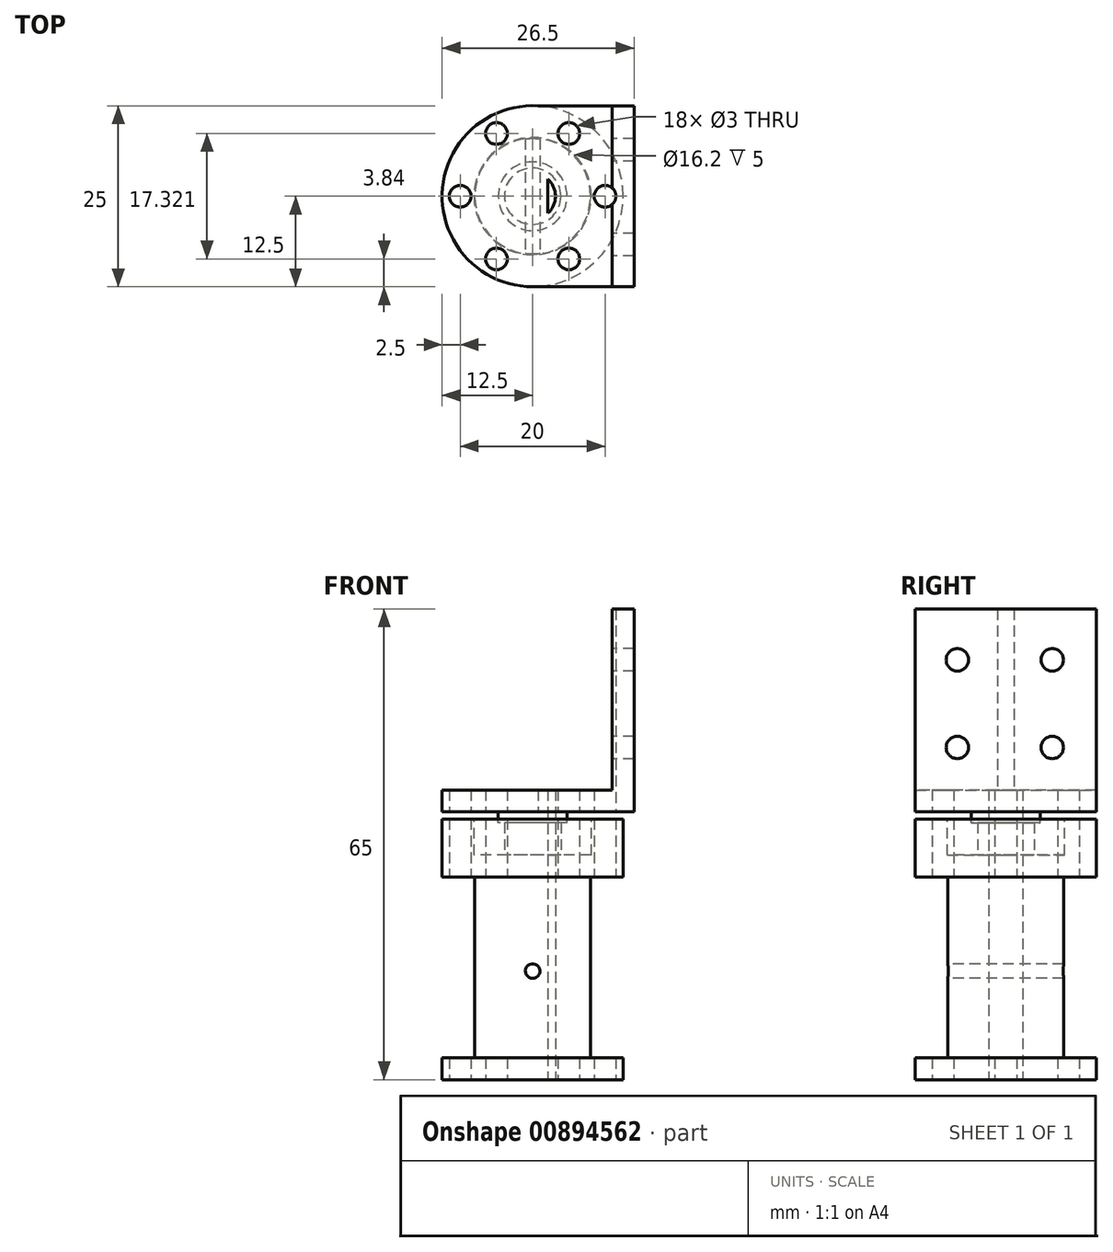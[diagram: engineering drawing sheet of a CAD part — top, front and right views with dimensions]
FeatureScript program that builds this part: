
annotation { "Feature Type Name" : "Feature", "Feature Type Description" : "" }
export const myFeature = defineFeature(function(context is Context, id is Id, definition is map)
    precondition{}
    {
        {
            var Q0;
            Q0=qCreatedBy(makeId("Top.planeOp"),FACE);
            var sketch = newSketch(context, id + "F0", { "sketchPlane" : qUnion([Q0])});
            skCircle(sketch, "E0", {"center": v(0, 0) * mm, "radius": 12.5 * mm});
            skLineSegment(sketch, "E1", {"start": v(0, 0) * mm, "end": v(10, 0) * mm, "construction": true});
            skCircle(sketch, "E2", {"center": v(10, 0) * mm, "radius": 1.5 * mm});
            skCircle(sketch, "E3.1.0", {"center": v(5, 8.66) * mm, "radius": 1.5 * mm});
            skCircle(sketch, "E3.2.0", {"center": v(-5, 8.66) * mm, "radius": 1.5 * mm});
            skCircle(sketch, "E3.3.0", {"center": v(-10, 0) * mm, "radius": 1.5 * mm});
            skCircle(sketch, "E3.4.0", {"center": v(-5, -8.66) * mm, "radius": 1.5 * mm});
            skCircle(sketch, "E3.5.0", {"center": v(5, -8.66) * mm, "radius": 1.5 * mm});
            skCircle(sketch, "E4", {"center": v(0, 0) * mm, "radius": 3.15 * mm});
            skLineSegment(sketch, "E5.bottom", {"start": v(2.1, -4.87) * mm, "end": v(-8.4, -4.87) * mm, "construction": true});
            skLineSegment(sketch, "E5.top", {"start": v(2.1, 4.87) * mm, "end": v(-8.4, 4.87) * mm, "construction": true});
            skLineSegment(sketch, "E5.left", {"start": v(2.1, -4.87) * mm, "end": v(2.1, 4.87) * mm});
            skLineSegment(sketch, "E5.right", {"start": v(-8.4, -4.87) * mm, "end": v(-8.4, 4.87) * mm, "construction": true});
            skPoint(sketch, "E5.middle", {"position": v(-3.15, 0) * mm});
            skSolve(sketch);
        }
        {
            var Q0;
            Q0=makeQuery(id+"F0.imprint","IMPRINT",FACE,{"disambiguationData":[TD([[makeQuery(id+"F0.imprint","IMPRINT",EDGE,{"derivedFrom":sQuery(id+"F0.wireOp",EDGE,"E0")}),1.0]])]});
            var Q1;
            {var subQ0=sQuery(id+"F0.wireOp",EDGE,"E5.left");var subQ1=sQuery(id+"F0.wireOp",EDGE,"E4");var subQ2=makeQuery(id+"F0.imprint","INTERSECT",VERTEX,{"disambiguationData":[OD(0.0)],"derivedFrom":[subQ1,subQ0]});Q1=makeQuery(id+"F0.imprint","IMPRINT",FACE,{"disambiguationData":[TD([[makeQuery(id+"F0.imprint","IMPRINT",EDGE,{"disambiguationData":[TD([[subQ2,-1.0]])],"derivedFrom":subQ1}),1.0]])]});}
            var Q2;
            Q2=makeQuery(id+"F0.imprint","IMPRINT",FACE,{"disambiguationData":[TD([[makeQuery(id+"F0.imprint","IMPRINT",EDGE,{"derivedFrom":sQuery(id+"F0.wireOp",EDGE,"I6GdOmMd-8NHa-Wv74-HRZH-CkJwQ5Tk9hPf")}),1.0]])]});
            extrude(context, id + "F1", {"entities" : qUnion([Q0, Q1, Q2]), "depth" : 3 * mm, "offsetDistance" : 25 * mm});
        }
        {
            var Q0;
            Q0=makeQuery(id+"F1.opExtrude","CAP_FACE",FACE,{"disambiguationData":[OSD([sQuery(id+"F0.wireOp",EDGE,"E0"),sQuery(id+"F0.wireOp",EDGE,"E2"),sQuery(id+"F0.wireOp",EDGE,"E3.1.0"),sQuery(id+"F0.wireOp",EDGE,"E3.2.0"),sQuery(id+"F0.wireOp",EDGE,"E3.3.0"),sQuery(id+"F0.wireOp",EDGE,"E3.4.0"),sQuery(id+"F0.wireOp",EDGE,"E3.5.0"),sQuery(id+"F0.wireOp",EDGE,"E4"),sQuery(id+"F0.wireOp",EDGE,"E5.left")])],"isStart":false});
            var sketch = newSketch(context, id + "F2", { "sketchPlane" : qUnion([Q0])});
            skCircle(sketch, "E6", {"center": v(0, 0) * mm, "radius": 8 * mm});
            skSolve(sketch);
        }
        {
            var Q0;
            Q0=makeQuery(id+"F2.imprint","IMPRINT",FACE,{"disambiguationData":[TD([[makeQuery(id+"F2.imprint","IMPRINT",EDGE,{"derivedFrom":sQuery(id+"F2.wireOp",EDGE,"E6")}),1.0]])]});
            extrude(context, id + "F3", {"entities" : qUnion([Q0]), "operationType" : NewBodyOperationType.ADD, "depth" : 25 * mm, "offsetDistance" : 25 * mm});
        }
        {
            var Q0;
            Q0=makeQuery(id+"F3.opExtrude","CAP_FACE",FACE,{"disambiguationData":[OSD([sQuery(id+"F0.wireOp",EDGE,"E4"),sQuery(id+"F0.wireOp",EDGE,"E5.left"),sQuery(id+"F2.wireOp",EDGE,"E6")])],"isStart":false});
            var sketch = newSketch(context, id + "F4", { "sketchPlane" : qUnion([Q0])});
            skCircle(sketch, "E7", {"center": v(0, 0) * mm, "radius": 12.5 * mm});
            skCircle(sketch, "E8", {"center": v(0, 0) * mm, "radius": 8.1 * mm});
            skSolve(sketch);
        }
        {
            var Q0;
            Q0=makeQuery(id+"F4.imprint","IMPRINT",FACE,{"disambiguationData":[TD([[makeQuery(id+"F4.imprint","IMPRINT",EDGE,{"derivedFrom":makeQuery(id+"F3.opExtrude","CAP_EDGE",EDGE,{"disambiguationData":[OSD([sQuery(id+"F2.wireOp",EDGE,"E6")])],"isStart":false})}),1.0]])]});
            var Q1;
            Q1=makeQuery(id+"F4.imprint","IMPRINT",FACE,{"disambiguationData":[TD([[makeQuery(id+"F4.imprint","IMPRINT",EDGE,{"derivedFrom":sQuery(id+"F4.wireOp",EDGE,"E8")}),1.0]])]});
            var Q2;
            Q2=makeQuery(id+"F4.imprint","IMPRINT",FACE,{"disambiguationData":[TD([[makeQuery(id+"F4.imprint","IMPRINT",EDGE,{"derivedFrom":sQuery(id+"F4.wireOp",EDGE,"E7")}),1.0]])]});
            extrude(context, id + "F5", {"entities" : qUnion([Q0, Q1, Q2]), "operationType" : NewBodyOperationType.ADD, "depth" : 8 * mm, "offsetDistance" : 25 * mm});
        }
        {
            var Q0;
            Q0=makeQuery(id+"F5.opExtrude","CAP_FACE",FACE,{"disambiguationData":[OSD([sQuery(id+"F0.wireOp",EDGE,"E4"),sQuery(id+"F0.wireOp",EDGE,"E5.left"),sQuery(id+"F4.wireOp",EDGE,"E7")])],"isStart":false});
            var sketch = newSketch(context, id + "F6", { "sketchPlane" : qUnion([Q0])});
            skCircle(sketch, "E9", {"center": v(0, 0) * mm, "radius": 8.1 * mm});
            skSolve(sketch);
        }
        {
            var Q0;
            Q0=makeQuery(id+"F6.imprint","IMPRINT",FACE,{"disambiguationData":[TD([[makeQuery(id+"F6.imprint","IMPRINT",EDGE,{"derivedFrom":sQuery(id+"F6.wireOp",EDGE,"E9")}),1.0]])]});
            extrude(context, id + "F7", {"entities" : qUnion([Q0]), "operationType" : NewBodyOperationType.REMOVE, "oppositeDirection" : true, "depth" : 5 * mm, "offsetDistance" : 25 * mm});
        }
        {
            var Q0;
            Q0=qCreatedBy(makeId("Front.planeOp"),FACE);
            var sketch = newSketch(context, id + "F8", { "sketchPlane" : qUnion([Q0])});
            skLineSegment(sketch, "E10", {"start": v(0, 0) * mm, "end": v(0, 15) * mm, "construction": true});
            skCircle(sketch, "E11", {"center": v(0, 15) * mm, "radius": 1 * mm});
            skSolve(sketch);
        }
        {
            var Q0;
            Q0=qSketchRegion(id+"F8",true);
            extrude(context, id + "F9", {"entities" : qUnion([Q0]), "operationType" : NewBodyOperationType.REMOVE, "endBound" : BoundingType.SYMMETRIC, "oppositeDirection" : true, "depth" : 80 * mm, "offsetDistance" : 25 * mm});
        }
        {
            var Q0;
            Q0=makeQuery(id+"F7.boolean.opBoolean","COPY",FACE,{"derivedFrom":makeQuery(id+"F7.opExtrude","CAP_FACE",FACE,{"disambiguationData":[OSD([sQuery(id+"F0.wireOp",EDGE,"E4"),sQuery(id+"F0.wireOp",EDGE,"E5.left"),sQuery(id+"F6.wireOp",EDGE,"E9")])],"isStart":false})});
            var sketch = newSketch(context, id + "F10", { "sketchPlane" : qUnion([Q0])});
            skCircle(sketch, "E12", {"center": v(0, 0) * mm, "radius": 3.9 * mm});
            skSolve(sketch);
        }
        {
            var Q0;
            Q0=makeQuery(id+"F10.imprint","IMPRINT",FACE,{"disambiguationData":[TD([[makeQuery(id+"F10.imprint","IMPRINT",EDGE,{"derivedFrom":sQuery(id+"F10.wireOp",EDGE,"E12")}),1.0]])]});
            var Q1;
            Q1=makeQuery(id+"F10.imprint","IMPRINT",FACE,{"disambiguationData":[TD([[makeQuery(id+"F10.imprint","IMPRINT",EDGE,{"derivedFrom":makeQuery(id+"F7.boolean.opBoolean","COPY",EDGE,{"derivedFrom":makeQuery(id+"F7.opExtrude","CAP_EDGE",EDGE,{"disambiguationData":[OSD([sQuery(id+"F0.wireOp",EDGE,"E4")])],"isStart":false})})}),1.0]])]});
            extrude(context, id + "F11", {"entities" : qUnion([Q0, Q1]), "depth" : 6 * mm, "offsetDistance" : 25 * mm});
        }
        {
            var Q0;
            Q0=makeQuery(id+"F11.opExtrude","CAP_FACE",FACE,{"disambiguationData":[OSD([sQuery(id+"F10.wireOp",EDGE,"E12")])],"isStart":false});
            var sketch = newSketch(context, id + "F12", { "sketchPlane" : qUnion([Q0])});
            skCircle(sketch, "E13", {"center": v(0, 0) * mm, "radius": 4.75 * mm});
            skSolve(sketch);
        }
        {
            var Q0;
            Q0=makeQuery(id+"F12.imprint","IMPRINT",FACE,{"disambiguationData":[TD([[makeQuery(id+"F12.imprint","IMPRINT",EDGE,{"derivedFrom":sQuery(id+"F12.wireOp",EDGE,"E13")}),1.0]])]});
            var Q1;
            Q1=makeQuery(id+"F12.imprint","IMPRINT",FACE,{"disambiguationData":[TD([[makeQuery(id+"F12.imprint","IMPRINT",EDGE,{"derivedFrom":makeQuery(id+"F11.opExtrude","CAP_EDGE",EDGE,{"disambiguationData":[OSD([sQuery(id+"F10.wireOp",EDGE,"E12")])],"isStart":false})}),1.0]])]});
            extrude(context, id + "F13", {"entities" : qUnion([Q0, Q1]), "operationType" : NewBodyOperationType.ADD, "oppositeDirection" : true, "depth" : 1.5 * mm, "offsetDistance" : 25 * mm});
        }
        {
            var Q0;
            Q0=makeQuery(id+"F11.opExtrude","CAP_FACE",FACE,{"disambiguationData":[OSD([sQuery(id+"F10.wireOp",EDGE,"E12")])],"isStart":false});
            var sketch = newSketch(context, id + "F14", { "sketchPlane" : qUnion([Q0])});
            skCircle(sketch, "E14", {"center": v(0, 0) * mm, "radius": 12.5 * mm});
            skLineSegment(sketch, "E15.bottom", {"start": v(0, -12.5) * mm, "end": v(14, -12.5) * mm});
            skLineSegment(sketch, "E15.top", {"start": v(0, 12.48) * mm, "end": v(14, 12.48) * mm});
            skLineSegment(sketch, "E15.right", {"start": v(14, -12.5) * mm, "end": v(14, 12.48) * mm});
            skSolve(sketch);
        }
        {
            var Q0;
            Q0=makeQuery(id+"F14.imprint","IMPRINT",FACE,{"disambiguationData":[TD([[makeQuery(id+"F14.imprint","IMPRINT",EDGE,{"derivedFrom":sQuery(id+"F14.wireOp",EDGE,"E14")}),1.0]])]});
            var Q1;
            Q1=makeQuery(id+"F14.imprint","IMPRINT",FACE,{"disambiguationData":[TD([[makeQuery(id+"F14.imprint","IMPRINT",EDGE,{"derivedFrom":makeQuery(id+"F11.opExtrude","CAP_EDGE",EDGE,{"disambiguationData":[OSD([sQuery(id+"F10.wireOp",EDGE,"E12")])],"isStart":false})}),1.0]])]});
            var Q2;
            Q2=makeQuery(id+"F14.imprint","IMPRINT",FACE,{"disambiguationData":[TD([[makeQuery(id+"F14.imprint","IMPRINT",EDGE,{"derivedFrom":makeQuery(id+"F13.opExtrude","CAP_EDGE",EDGE,{"disambiguationData":[OSD([sQuery(id+"F12.wireOp",EDGE,"E13")])],"isStart":true})}),1.0]])]});
            var Q3;
            {var subQ0=sQuery(id+"F14.wireOp",EDGE,"E15.bottom");Q3=makeQuery(id+"F14.imprint","IMPRINT",FACE,{"disambiguationData":[TD([[makeQuery(id+"F14.imprint","IMPRINT",EDGE,{"derivedFrom":subQ0}),1.0]])]});}
            extrude(context, id + "F15", {"entities" : qUnion([Q0, Q1, Q2, Q3]), "operationType" : NewBodyOperationType.ADD, "depth" : 3 * mm, "offsetDistance" : 25 * mm});
        }
        {
            var Q0;
            Q0=makeQuery(id+"F0.imprint","IMPRINT",FACE,{"disambiguationData":[TD([[makeQuery(id+"F0.imprint","IMPRINT",EDGE,{"derivedFrom":sQuery(id+"F0.wireOp",EDGE,"E3.2.0")}),1.0]])]});
            var Q1;
            Q1=makeQuery(id+"F0.imprint","IMPRINT",FACE,{"disambiguationData":[TD([[makeQuery(id+"F0.imprint","IMPRINT",EDGE,{"derivedFrom":sQuery(id+"F0.wireOp",EDGE,"E3.1.0")}),1.0]])]});
            var Q2;
            Q2=makeQuery(id+"F0.imprint","IMPRINT",FACE,{"disambiguationData":[TD([[makeQuery(id+"F0.imprint","IMPRINT",EDGE,{"derivedFrom":sQuery(id+"F0.wireOp",EDGE,"E2")}),1.0]])]});
            var Q3;
            Q3=makeQuery(id+"F0.imprint","IMPRINT",FACE,{"disambiguationData":[TD([[makeQuery(id+"F0.imprint","IMPRINT",EDGE,{"derivedFrom":sQuery(id+"F0.wireOp",EDGE,"E3.5.0")}),1.0]])]});
            var Q4;
            Q4=makeQuery(id+"F0.imprint","IMPRINT",FACE,{"disambiguationData":[TD([[makeQuery(id+"F0.imprint","IMPRINT",EDGE,{"derivedFrom":sQuery(id+"F0.wireOp",EDGE,"E3.4.0")}),1.0]])]});
            var Q5;
            Q5=makeQuery(id+"F0.imprint","IMPRINT",FACE,{"disambiguationData":[TD([[makeQuery(id+"F0.imprint","IMPRINT",EDGE,{"derivedFrom":sQuery(id+"F0.wireOp",EDGE,"E3.3.0")}),1.0]])]});
            var Q6;
            Q6=sQuery(id+"F0.wireOp",EDGE,"E3.2.0");
            var Q7;
            Q7=sQuery(id+"F0.wireOp",EDGE,"E3.1.0");
            var Q8;
            Q8=sQuery(id+"F0.wireOp",EDGE,"E2");
            var Q9;
            Q9=sQuery(id+"F0.wireOp",EDGE,"E3.5.0");
            var Q10;
            Q10=sQuery(id+"F0.wireOp",EDGE,"E3.4.0");
            var Q11;
            Q11=sQuery(id+"F0.wireOp",EDGE,"E3.3.0");
            extrude(context, id + "F16", {"entities" : qUnion([Q0, Q1, Q2, Q3, Q4, Q5]), "operationType" : NewBodyOperationType.REMOVE, "surfaceEntities" : qUnion([Q6, Q7, Q8, Q9, Q10, Q11]), "endBound" : BoundingType.THROUGH_ALL, "depth" : 25 * mm, "offsetDistance" : 25 * mm});
        }
        {
            var Q0;
            Q0=makeQuery(id+"F15.opExtrude","CAP_FACE",FACE,{"disambiguationData":[OSD([sQuery(id+"F14.wireOp",EDGE,"E14"),sQuery(id+"F14.wireOp",EDGE,"E15.bottom"),sQuery(id+"F14.wireOp",EDGE,"E15.top"),sQuery(id+"F14.wireOp",EDGE,"E15.right")])],"isStart":false});
            var sketch = newSketch(context, id + "F17", { "sketchPlane" : qUnion([Q0])});
            skLineSegment(sketch, "E16.bottom", {"start": v(14, -12.5) * mm, "end": v(11, -12.5) * mm});
            skLineSegment(sketch, "E16.top", {"start": v(14, 12.48) * mm, "end": v(11, 12.48) * mm});
            skLineSegment(sketch, "E16.left", {"start": v(14, -12.5) * mm, "end": v(14, 12.48) * mm});
            skLineSegment(sketch, "E16.right", {"start": v(11, -12.5) * mm, "end": v(11, 12.48) * mm});
            skSolve(sketch);
        }
        {
            var Q0;
            {var subQ1=sQuery(id+"F17.wireOp",EDGE,"E16.bottom");Q0=makeQuery(id+"F17.imprint","IMPRINT",FACE,{"disambiguationData":[TD([[makeQuery(id+"F17.imprint","IMPRINT",EDGE,{"derivedFrom":subQ1}),1.0]])]});}
            extrude(context, id + "F18", {"entities" : qUnion([Q0]), "operationType" : NewBodyOperationType.ADD, "depth" : 25 * mm, "offsetDistance" : 25 * mm});
        }
        {
            var Q0;
            {var subQ0=sQuery(id+"F17.wireOp",EDGE,"E16.right");var subQ1=sQuery(id+"F14.wireOp",EDGE,"E15.top");Q0=makeQuery(id+"F18.opExtrude","SWEPT_FACE",FACE,{"disambiguationData":[OSD([subQ0]),TDD([makeQuery(id+"F17.imprint","IMPRINT",EDGE,{"disambiguationData":[TD([[makeQuery(id+"F17.imprint","INTERSECT",VERTEX,{"derivedFrom":[makeQuery(id+"F15.opExtrude","CAP_EDGE",EDGE,{"disambiguationData":[OSD([subQ1])],"isStart":false}),sQuery(id+"F17.wireOp",EDGE,"E16.top"),subQ0]}),1.0]])],"derivedFrom":subQ0})])]});}
            var sketch = newSketch(context, id + "F19", { "sketchPlane" : qUnion([Q0])});
            skCircle(sketch, "E17", {"center": v(-6.41, 45.88) * mm, "radius": 1.55 * mm});
            skCircle(sketch, "E18.0.1.0", {"center": v(-6.41, 57.98) * mm, "radius": 1.55 * mm});
            skCircle(sketch, "E18.1.0.0", {"center": v(6.69, 45.88) * mm, "radius": 1.55 * mm});
            skCircle(sketch, "E18.1.1.0", {"center": v(6.69, 57.98) * mm, "radius": 1.55 * mm});
            skLineSegment(sketch, "E18.direction1", {"start": v(-6.41, 45.88) * mm, "end": v(6.69, 45.88) * mm, "construction": true});
            skLineSegment(sketch, "E18.direction2", {"start": v(-6.41, 45.88) * mm, "end": v(-6.41, 57.98) * mm, "construction": true});
            skSolve(sketch);
        }
        {
            var Q0;
            Q0=qSketchRegion(id+"F19",true);
            extrude(context, id + "F20", {"entities" : qUnion([Q0]), "operationType" : NewBodyOperationType.REMOVE, "oppositeDirection" : true, "depth" : 25 * mm, "offsetDistance" : 25 * mm});
        }
    });
